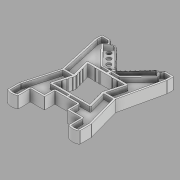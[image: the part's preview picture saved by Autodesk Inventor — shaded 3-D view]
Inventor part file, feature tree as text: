
AUTODESK INVENTOR PART (.ipt)
format: ipt  version: 2022.1 (Build 261234020, 234B)  size: 3,039,744 bytes
history: native  units: in
note: dims shown in document units (in); Inventor stores cm internally (conversion verified against a paired STEP export)
features: extrude x7, sketch x5, chamfer x4, mirror x4, plane x4, fillet x3, boolean_combine x3, other x1, projected_geometry x1
ambient origin geometry x8: Origin, YZ Plane, XZ Plane, XY Plane, X Axis, Y Axis, Z Axis, Center Point
bodies: Solid1 (feature_tree), Solid2 (feature_tree), Solid3 (feature_tree), Solid4 (feature_tree)
feature tree (32):
  sketch  "Sketch1"  dims[d7=7.9381in d16=3.1568in]
  extrude  "Extrusion1"  Depth=3.1568in
  extrude  "Extrusion2"  Depth=0.6164in
  extrude  "Extrusion3"  Depth=0.7283in
  extrude  "Extrusion4"  Depth=0.6398in
  chamfer  "Chamfer1"  Distance=0.0197in
  chamfer  "Chamfer2"  Distance=0.0266in
  chamfer  "Chamfer3"  Distance=0.7677in
  chamfer  "Chamfer4"  Distance=0.748in
  sketch  "Sketch2"  dims[d17=2.5927in d29=0.6164in]
  fillet  "Fillet1"  Radius=0.0659in
  fillet  "Fillet2"  Radius=0.0659in
  fillet  "Fillet3"  Radius=0.748in
  extrude  "Extrusion5"  Depth=0.0236in
  mirror  "Mirror1"
  boolean_combine  "Combine1"
  extrude  "Extrusion6"  Depth=0.0236in
  plane  "Work Plane1"
  mirror  "Mirror2"
  boolean_combine  "Combine2"
  plane  "Work Plane4"
  extrude  "Extrusion7"  Depth=0.0236in
  mirror  "Mirror3"
  mirror  "Mirror4"
  boolean_combine  "Combine3"
  other  "Image1"
  sketch  "Sketch3"  dims[d31=1.9685in d37=0.7283in]
  sketch  "Sketch4"  dims[d38=0.0276in d39=0.6398in]
  plane  "Work Plane2"
  plane  "Work Plane3"
  sketch  "Sketch5"  dims[d40=0.9173in d41=0.0197in d42=0.0266in d43=0.7677in d44=0.748in d45=0.0659in d46=0.0659in d47=0.748in d48=0.187in d49=2.2441in d50=2.8543in d51=0.3839in d52=0.4528in d53=0.0591in d54=0.1575in d55=0.1903in d56=0.1476in d57=1.0429in d58=0.1634in d59=0.0787in d61=2.9211in d62=0.4426in d78=0.1181in d92=0.0787in d114=0.1378in d128=0.0591in d129=0.1181in d139=0.0787in d148=0.1378in d149=1.7913in d150=0.1575in d151=0.0827in d159=0.0787in d162=0.0787in d164=0.0591in d166=0.0787in d245=0.0594in d246=0.7049in d247=0.3055in d248=0.9271in d249=0.8975in d250=0.3097in d251=0.923in d252=0.7244in d253=0.0in d254=1.851in d255=1.4294in d256=1.2977in d257=3.6187in d258=0.0737in d259=2.5252in d260=0.1721in d261=0.1181in d262=0.0984in d263=1.9073in d264=2.0451in d265=2.3942in d266=0.0364in d267=2.309in d268=4.4539in d269=4.3714in d270=1.466in d271=1.466in d272=1.8095in d273=4.2023in d274=1.2451in d275=1.4789in d276=3.157in d277=3.1585in d279=0.3051in d281=1.5748in d283=0.4724in d284=0.3937in d286=0.3937in d292=0.328in d293=1.4776in d294=1.4695in d296=0.1181in d297=0.0in d308=0.7874in d309=0.0in d310=0.4331in d311=0.0in d312=0.0787in d313=0.1575in d314=0.4331in d315=0.0in d316=0.1772in d317=0.0787in d318=45.0deg d319=0.1772in d320=0.0787in d321=45.0deg d322=0.2505in d323=0.0787in d324=45.0deg d325=0.2295in d326=0.0787in d327=45.0deg d328=0.0787in d329=0.0787in d330=0.8484in d331=0.0551in d332=3.1496in d334=0.2362in d335=0.3937in d337=0.3937in d339=0.0394in d340=0.0in d341=0.4921in d342=0.8071in d343=0.4921in d344=0.8071in d345=0.063in d346=0.7874in d347=0.063in d348=0.7874in d349=0.063in d350=0.7874in d351=0.063in d352=0.7874in d353=0.0236in d354=0.0in d355=0.1378in d356=0.2953in d357=0.2953in d358=0.0591in d359=0.7874in d360=0.0591in d361=0.7874in d362=0.0591in d363=0.7874in d364=0.0236in d365=0.0in]
  projected_geometry  "Projected Loop1"
